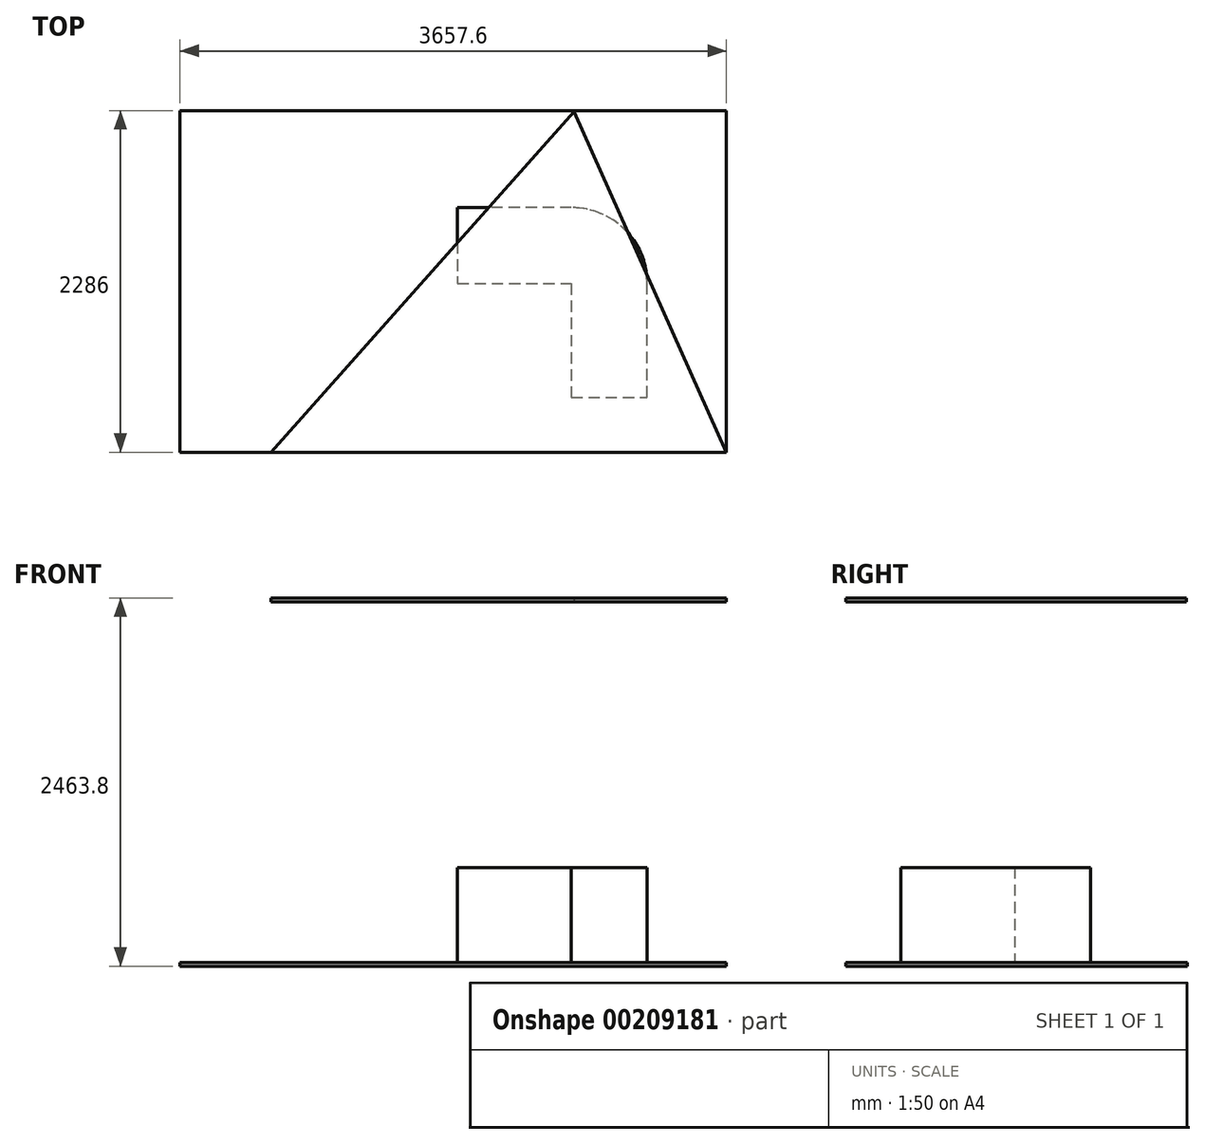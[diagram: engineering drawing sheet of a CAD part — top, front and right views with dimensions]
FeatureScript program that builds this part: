
annotation { "Feature Type Name" : "Feature", "Feature Type Description" : "" }
export const myFeature = defineFeature(function(context is Context, id is Id, definition is map)
    precondition{}
    {
        {
            var Q0;
            Q0=qCreatedBy(makeId("Top.planeOp"),FACE);
            var sketch = newSketch(context, id + "F0", { "sketchPlane" : qUnion([Q0])});
            skLineSegment(sketch, "E0.bottom", {"start": v(-1933.76, -1150.85) * mm, "end": v(1723.84, -1150.85) * mm});
            skLineSegment(sketch, "E0.top", {"start": v(-1933.76, 1135.15) * mm, "end": v(1723.84, 1135.15) * mm});
            skLineSegment(sketch, "E0.left", {"start": v(-1933.76, -1150.85) * mm, "end": v(-1933.76, 1135.15) * mm});
            skLineSegment(sketch, "E0.right", {"start": v(1723.84, -1150.85) * mm, "end": v(1723.84, 1135.15) * mm});
            skSolve(sketch);
        }
        {
            var Q0;
            Q0=makeQuery(id+"F0.imprint","IMPRINT",FACE,{"disambiguationData":[TD([[makeQuery(id+"F0.imprint","IMPRINT",EDGE,{"derivedFrom":sQuery(id+"F0.wireOp",EDGE,"E0.bottom")}),1.0]])]});
            extrude(context, id + "F1", {"entities" : qUnion([Q0]), "depth" : 25.4 * mm});
        }
        {
            var Q0;
            Q0=makeQuery(id+"F1.opExtrude","CAP_FACE",FACE,{"disambiguationData":[OSD([sQuery(id+"F0.wireOp",EDGE,"E0.bottom"),sQuery(id+"F0.wireOp",EDGE,"E0.top"),sQuery(id+"F0.wireOp",EDGE,"E0.left"),sQuery(id+"F0.wireOp",EDGE,"E0.right")])],"isStart":false});
            var sketch = newSketch(context, id + "F2", { "sketchPlane" : qUnion([Q0])});
            skArc(sketch, "E1", {"start": v(1193.1, -22.16) * mm, "mid": v(1044.31, 337.06) * mm, "end": v(685.1, 485.84) * mm});
            skLineSegment(sketch, "E2", {"start": v(685.1, 485.84) * mm, "end": v(-76.9, 485.84) * mm});
            skLineSegment(sketch, "E3", {"start": v(-76.9, 485.84) * mm, "end": v(-76.9, -22.16) * mm});
            skLineSegment(sketch, "E4", {"start": v(-76.9, -22.16) * mm, "end": v(685.1, -22.16) * mm});
            skLineSegment(sketch, "E5", {"start": v(685.1, -784.16) * mm, "end": v(1193.1, -784.16) * mm});
            skLineSegment(sketch, "E6", {"start": v(1193.1, -784.16) * mm, "end": v(1193.1, -22.16) * mm});
            skLineSegment(sketch, "E7", {"start": v(685.1, -22.16) * mm, "end": v(685.1, -784.16) * mm});
            skSolve(sketch);
        }
        {
            var Q0;
            Q0=makeQuery(id+"F1.opExtrude","CAP_FACE",FACE,{"disambiguationData":[OSD([sQuery(id+"F0.wireOp",EDGE,"E0.bottom"),sQuery(id+"F0.wireOp",EDGE,"E0.top"),sQuery(id+"F0.wireOp",EDGE,"E0.left"),sQuery(id+"F0.wireOp",EDGE,"E0.right")])],"isStart":false});
            var sketch = newSketch(context, id + "F3", { "sketchPlane" : qUnion([Q0])});
            skCircle(sketch, "E8", {"center": v(-638.87, 154) * mm, "radius": 1250 * mm});
            skSolve(sketch);
        }
        {
            var Q0;
            Q0 = qSketchRegion(id + "F2", true);
            extrude(context, id + "F4", {"entities" : qUnion([Q0]), "operationType" : NewBodyOperationType.ADD, "depth" : 635 * mm});
        }
        {
            var Q0;
            Q0=qCreatedBy(makeId("Top.planeOp"),FACE);
            cPlane(context, id + "F5", {"entities" : qUnion([Q0]), "cplaneType" : CPlaneType.OFFSET, "offset" : 2438.4 * mm, "width" : 152.4 * mm, "height" : 152.4 * mm});
        }
        {
            var Q0;
            Q0=qCreatedBy(id+"F5.planeOp",FACE);
            var sketch = newSketch(context, id + "F6", { "sketchPlane" : qUnion([Q0])});
            skLineSegment(sketch, "E9", {"start": v(1723.84, -1150.85) * mm, "end": v(701.52, 1126.64) * mm});
            skLineSegment(sketch, "E10", {"start": v(701.52, 1126.64) * mm, "end": v(-1324.16, -1150.85) * mm});
            skLineSegment(sketch, "E11", {"start": v(-1324.16, -1150.85) * mm, "end": v(1723.84, -1150.85) * mm});
            skSolve(sketch);
        }
        {
            var Q0;
            Q0=makeQuery(id+"F6.imprint","IMPRINT",FACE,{"disambiguationData":[TD([[makeQuery(id+"F6.imprint","IMPRINT",EDGE,{"derivedFrom":sQuery(id+"F6.wireOp",EDGE,"E9")}),1.0]])]});
            extrude(context, id + "F7", {"entities" : qUnion([Q0]), "depth" : 25.4 * mm});
        }
    });
